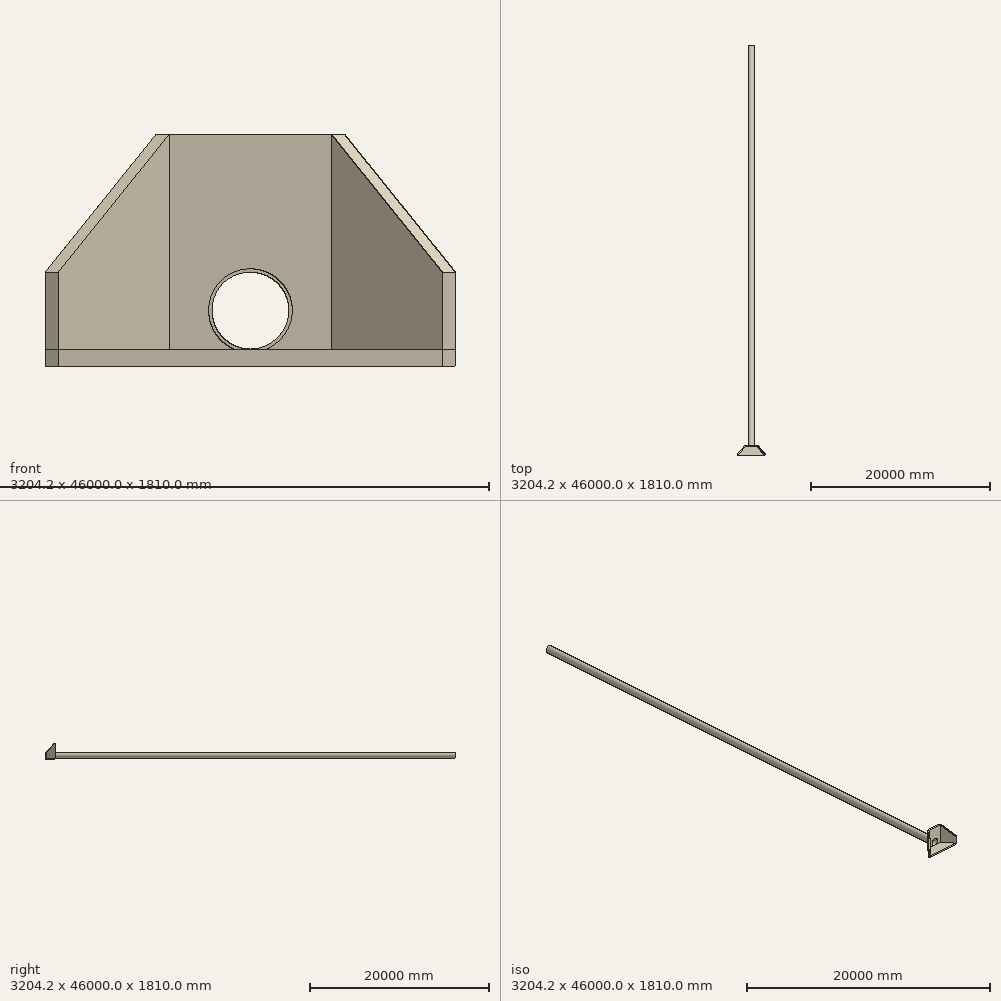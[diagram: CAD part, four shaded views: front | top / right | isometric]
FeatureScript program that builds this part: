
annotation { "Feature Type Name" : "Feature", "Feature Type Description" : "" }
export const myFeature = defineFeature(function(context is Context, id is Id, definition is map)
    precondition{}
    {
        {
            assignVariable(context, id + "F0", {"name" : "HeadwallThickness_t", "anyValue" : 135});
        }
        {
            assignVariable(context, id + "F1", {"name" : "PipeLength", "anyValue" : 45000});
        }
        {
            var Q0;
            Q0=qCreatedBy(makeId("Front.planeOp"),FACE);
            var sketch = newSketch(context, id + "F2", { "sketchPlane" : qUnion([Q0])});
            skCircle(sketch, "E0", {"center": v(0, 300) * mm, "radius": 300 * mm});
            skCircle(sketch, "E1", {"center": v(0, 300) * mm, "radius": 327 * mm});
            skSolve(sketch);
        }
        {
            var Q0;
            {var subQ0=sQuery(id+"F2.wireOp",EDGE,"E0");Q0=makeQuery(id+"F2.imprint","IMPRINT",FACE,{"disambiguationData":[TD([[makeQuery(id+"F2.imprint","IMPRINT",EDGE,{"derivedFrom":subQ0}),-1.0]])]});}
            extrude(context, id + "F3", {"entities" : qUnion([Q0]), "oppositeDirection" : true, "depth" : (getVariable(context, 'PipeLength')) * mm, "offsetDistance" : 25 * mm});
        }
        {
            var Q0;
            Q0=qCreatedBy(makeId("Front.planeOp"),FACE);
            var sketch = newSketch(context, id + "F4", { "sketchPlane" : qUnion([Q0])});
            skLineSegment(sketch, "E2.bottom", {"start": v(-635, 1675) * mm, "end": v(635, 1675) * mm});
            skLineSegment(sketch, "E2.top", {"start": v(-635, 0) * mm, "end": v(635, 0) * mm});
            skLineSegment(sketch, "E2.left", {"start": v(-635, 1675) * mm, "end": v(-635, 0) * mm});
            skLineSegment(sketch, "E2.right", {"start": v(635, 1675) * mm, "end": v(635, 0) * mm});
            skCircle(sketch, "E3.0", {"center": v(0, 300) * mm, "radius": 327 * mm});
            skSolve(sketch);
        }
        {
            var Q0;
            Q0=makeQuery(id+"F4.imprint","IMPRINT",FACE,{"disambiguationData":[TD([[makeQuery(id+"F4.imprint","IMPRINT",EDGE,{"derivedFrom":sQuery(id+"F4.wireOp",EDGE,"E2.bottom")}),-1.0]])]});
            extrude(context, id + "F5", {"entities" : qUnion([Q0]), "oppositeDirection" : true, "depth" : (getVariable(context, 'HeadwallThickness_t')) * mm, "offsetDistance" : 25 * mm});
        }
        {
            var Q0;
            Q0=qCreatedBy(makeId("Top.planeOp"),FACE);
            var sketch = newSketch(context, id + "F6", { "sketchPlane" : qUnion([Q0])});
            skLineSegment(sketch, "E4.0", {"start": v(-635, 0) * mm, "end": v(635, 0) * mm});
            skLineSegment(sketch, "E5", {"start": v(-1500, -1000) * mm, "end": v(1500, -1000) * mm});
            skLineSegment(sketch, "E6", {"start": v(0, 0) * mm, "end": v(0, -1000) * mm, "construction": true});
            skLineSegment(sketch, "E7", {"start": v(-635, 0) * mm, "end": v(-1500, -1000) * mm});
            skLineSegment(sketch, "E8", {"start": v(635, 0) * mm, "end": v(1500, -1000) * mm});
            skSolve(sketch);
        }
        {
            var Q0;
            Q0=makeQuery(id+"F6.imprint","IMPRINT",FACE,{"disambiguationData":[TD([[makeQuery(id+"F6.imprint","IMPRINT",EDGE,{"derivedFrom":sQuery(id+"F6.wireOp",EDGE,"E4.0")}),-1.0]])]});
            extrude(context, id + "F7", {"entities" : qUnion([Q0]), "oppositeDirection" : true, "depth" : (getVariable(context, 'HeadwallThickness_t')) * mm, "offsetDistance" : 25 * mm});
        }
        {
            var Q0;
            Q0=makeQuery(id+"F7.opExtrude","CAP_EDGE",EDGE,{"disambiguationData":[OSD([sQuery(id+"F6.wireOp",EDGE,"E8")])],"isStart":true});
            var Q1;
            Q1=makeQuery(id+"F7.opExtrude","CAP_VERTEX",VERTEX,{"disambiguationData":[OSD([sQuery(id+"F6.wireOp",EDGE,"E5"),sQuery(id+"F6.wireOp",EDGE,"E8")])],"isStart":true});
            cPlane(context, id + "F8", {"entities" : qUnion([Q0, Q1]), "cplaneType" : CPlaneType.LINE_POINT, "offset" : 25 * mm, "width" : 150 * mm, "height" : 150 * mm});
        }
        {
            var Q0;
            Q0=qCreatedBy(id+"F8.planeOp",FACE);
            var sketch = newSketch(context, id + "F9", { "sketchPlane" : qUnion([Q0])});
            skPoint(sketch, "E9.0", {"position": v(480.26, 0) * mm});
            skLineSegment(sketch, "E10.bottom", {"start": v(480.26, 0) * mm, "end": v(615.26, 0) * mm});
            skLineSegment(sketch, "E10.top", {"start": v(480.26, 600) * mm, "end": v(615.26, 600) * mm});
            skLineSegment(sketch, "E10.left", {"start": v(480.26, 0) * mm, "end": v(480.26, 600) * mm});
            skLineSegment(sketch, "E10.right", {"start": v(615.26, 0) * mm, "end": v(615.26, 600) * mm});
            skSolve(sketch);
        }
        {
            var Q0;
            Q0=makeQuery(id+"F7.opExtrude","CAP_EDGE",EDGE,{"disambiguationData":[OSD([sQuery(id+"F6.wireOp",EDGE,"E8")])],"isStart":true});
            var Q1;
            Q1=makeQuery(id+"F5.opExtrude","CAP_VERTEX",VERTEX,{"disambiguationData":[OSD([sQuery(id+"F4.wireOp",EDGE,"E2.top"),sQuery(id+"F4.wireOp",EDGE,"E2.right")])],"isStart":true});
            cPlane(context, id + "F10", {"entities" : qUnion([Q0, Q1]), "cplaneType" : CPlaneType.LINE_POINT, "offset" : 25 * mm, "width" : 150 * mm, "height" : 150 * mm});
        }
        {
            var Q0;
            Q0=qCreatedBy(id+"F10.planeOp",FACE);
            var sketch = newSketch(context, id + "F11", { "sketchPlane" : qUnion([Q0])});
            skPoint(sketch, "E11.0", {"position": v(480.26, 0) * mm});
            skLineSegment(sketch, "E12.bottom", {"start": v(480.26, 0) * mm, "end": v(615.26, 0) * mm});
            skLineSegment(sketch, "E12.top", {"start": v(480.26, 1675) * mm, "end": v(615.26, 1675) * mm});
            skLineSegment(sketch, "E12.left", {"start": v(480.26, 0) * mm, "end": v(480.26, 1675) * mm});
            skLineSegment(sketch, "E12.right", {"start": v(615.26, 0) * mm, "end": v(615.26, 1675) * mm});
            skSolve(sketch);
        }
        {
            var Q0;
            Q0=makeQuery(id+"F9.imprint","IMPRINT",FACE,{"disambiguationData":[TD([[makeQuery(id+"F9.imprint","IMPRINT",EDGE,{"derivedFrom":sQuery(id+"F9.wireOp",EDGE,"E10.bottom")}),1.0]])]});
            var Q1;
            Q1=makeQuery(id+"F11.imprint","IMPRINT",FACE,{"disambiguationData":[TD([[makeQuery(id+"F11.imprint","IMPRINT",EDGE,{"derivedFrom":sQuery(id+"F11.wireOp",EDGE,"E12.bottom")}),1.0]])]});
            loft(context, id + "F12", {"sheetProfilesArray" : [{ "sheetProfileEntities" : qUnion([Q0]) }, { "sheetProfileEntities" : qUnion([Q1]) }]});
        }
        {
            var Q0;
            Q0=makeQuery(id+"F5.opExtrude","SWEPT_FACE",FACE,{"disambiguationData":[OSD([sQuery(id+"F4.wireOp",EDGE,"E2.bottom")])]});
            var sketch = newSketch(context, id + "F13", { "sketchPlane" : qUnion([Q0])});
            skLineSegment(sketch, "E13.0", {"start": v(-635, 135) * mm, "end": v(635, 135) * mm});
            skLineSegment(sketch, "E14.0", {"start": v(1602.1, -911.68) * mm, "end": v(737.1, 88.32) * mm});
            skArc(sketch, "E15", {"start": v(635, 135) * mm, "mid": v(691.13, 122.78) * mm, "end": v(737.1, 88.32) * mm});
            skSolve(sketch);
        }
        {
            var Q0;
            Q0=sQuery(id+"F13.wireOp",EDGE,"E15");
            var Q1;
            Q1=makeQuery(id+"F12.opLoft","CAP_FACE",FACE,{"disambiguationData":[OSD([makeQuery(id+"F11.imprint","IMPRINT",FACE,{"disambiguationData":[TD([[makeQuery(id+"F11.imprint","IMPRINT",EDGE,{"derivedFrom":sQuery(id+"F11.wireOp",EDGE,"E12.bottom")}),1.0]])]})])],"isStart":true});
            var Q2;
            Q2=makeQuery(id+"F5.opExtrude","SWEPT_FACE",FACE,{"disambiguationData":[OSD([sQuery(id+"F4.wireOp",EDGE,"E2.right")])]});
            loft(context, id + "F14", {"addSections" : true, "spine" : qUnion([Q0]), "sectionCount" : 5, "sheetProfilesArray" : [{ "sheetProfileEntities" : qUnion([Q1]) }, { "sheetProfileEntities" : qUnion([Q2]) }]});
        }
        {
            var Q0;
            Q0=makeQuery(id+"F12.opLoft","SWEPT_BODY",BODY,{"disambiguationData":[OSD([makeQuery(id+"F9.imprint","IMPRINT",FACE,{"disambiguationData":[TD([[makeQuery(id+"F9.imprint","IMPRINT",EDGE,{"derivedFrom":sQuery(id+"F9.wireOp",EDGE,"E10.bottom")}),1.0]])]}),makeQuery(id+"F11.imprint","IMPRINT",FACE,{"disambiguationData":[TD([[makeQuery(id+"F11.imprint","IMPRINT",EDGE,{"derivedFrom":sQuery(id+"F11.wireOp",EDGE,"E12.bottom")}),1.0]])]})])]});
            var Q1;
            Q1=makeQuery(id+"F14.opLoft","SWEPT_BODY",BODY,{"disambiguationData":[OSD([sQuery(id+"F4.wireOp",EDGE,"E2.right"),makeQuery(id+"F11.imprint","IMPRINT",FACE,{"disambiguationData":[TD([[makeQuery(id+"F11.imprint","IMPRINT",EDGE,{"derivedFrom":sQuery(id+"F11.wireOp",EDGE,"E12.bottom")}),1.0]])]})])]});
            var Q2;
            Q2=qCreatedBy(makeId("Right.planeOp"),FACE);
            mirror(context, id + "F15", {"operationType" : NewBodyOperationType.ADD, "entities" : qUnion([Q0, Q1]), "mirrorPlane" : qUnion([Q2])});
        }
        {
            var Q0;
            Q0=makeQuery(id+"F7.opExtrude","CAP_FACE",FACE,{"disambiguationData":[OSD([sQuery(id+"F6.wireOp",EDGE,"E4.0"),sQuery(id+"F6.wireOp",EDGE,"E5"),sQuery(id+"F6.wireOp",EDGE,"E7"),sQuery(id+"F6.wireOp",EDGE,"E8")])],"isStart":false});
            var sketch = newSketch(context, id + "F16", { "sketchPlane" : qUnion([Q0])});
            skLineSegment(sketch, "E16.0", {"start": v(-1500, 1000) * mm, "end": v(1500, 1000) * mm});
            skLineSegment(sketch, "E17.0", {"start": v(1602.1, 911.68) * mm, "end": v(1500, 1000) * mm});
            skLineSegment(sketch, "E18.0", {"start": v(1602.1, 911.68) * mm, "end": v(737.1, -88.32) * mm});
            skFitSpline(sketch, "E19.0", {"points": [v(737.1, -88.32) * mm, v(732.53, -93.13) * mm, v(722.72, -103.43) * mm, v(708.42, -113.73) * mm, v(691.3, -123.25) * mm, v(673.2, -129.92) * mm, v(654.3, -134.2) * mm, v(641.43, -134.74) * mm, v(635, -135) * mm]});
            skLineSegment(sketch, "E20.0", {"start": v(130.11, -135) * mm, "end": v(635, -135) * mm});
            skLineSegment(sketch, "E21.0", {"start": v(-635, -135) * mm, "end": v(-130.11, -135) * mm});
            skFitSpline(sketch, "E22.0", {"points": [v(-737.1, -88.32) * mm, v(-732.53, -93.13) * mm, v(-722.72, -103.43) * mm, v(-708.42, -113.73) * mm, v(-691.3, -123.25) * mm, v(-673.2, -129.92) * mm, v(-654.3, -134.2) * mm, v(-641.43, -134.74) * mm, v(-635, -135) * mm]});
            skLineSegment(sketch, "E23.0", {"start": v(-1602.1, 911.68) * mm, "end": v(-737.1, -88.32) * mm});
            skLineSegment(sketch, "E24.0", {"start": v(-1602.1, 911.68) * mm, "end": v(-1500, 1000) * mm});
            skLineSegment(sketch, "E25", {"start": v(-130.11, -135) * mm, "end": v(130.11, -135) * mm});
            skSolve(sketch);
        }
        {
            var Q0;
            Q0=makeQuery(id+"F16.imprint","IMPRINT",FACE,{"disambiguationData":[TD([[makeQuery(id+"F16.imprint","IMPRINT",EDGE,{"derivedFrom":sQuery(id+"F16.wireOp",EDGE,"E17.0")}),1.0]])]});
            var Q1;
            Q1=makeQuery(id+"F7.opExtrude","CAP_FACE",FACE,{"disambiguationData":[OSD([sQuery(id+"F6.wireOp",EDGE,"E4.0"),sQuery(id+"F6.wireOp",EDGE,"E5"),sQuery(id+"F6.wireOp",EDGE,"E7"),sQuery(id+"F6.wireOp",EDGE,"E8")])],"isStart":true});
            extrude(context, id + "F17", {"entities" : qUnion([Q0]), "endBound" : BoundingType.UP_TO_SURFACE, "oppositeDirection" : true, "depth" : 25 * mm, "endBoundEntityFace" : qUnion([Q1]), "offsetDistance" : 25 * mm});
        }
    });
